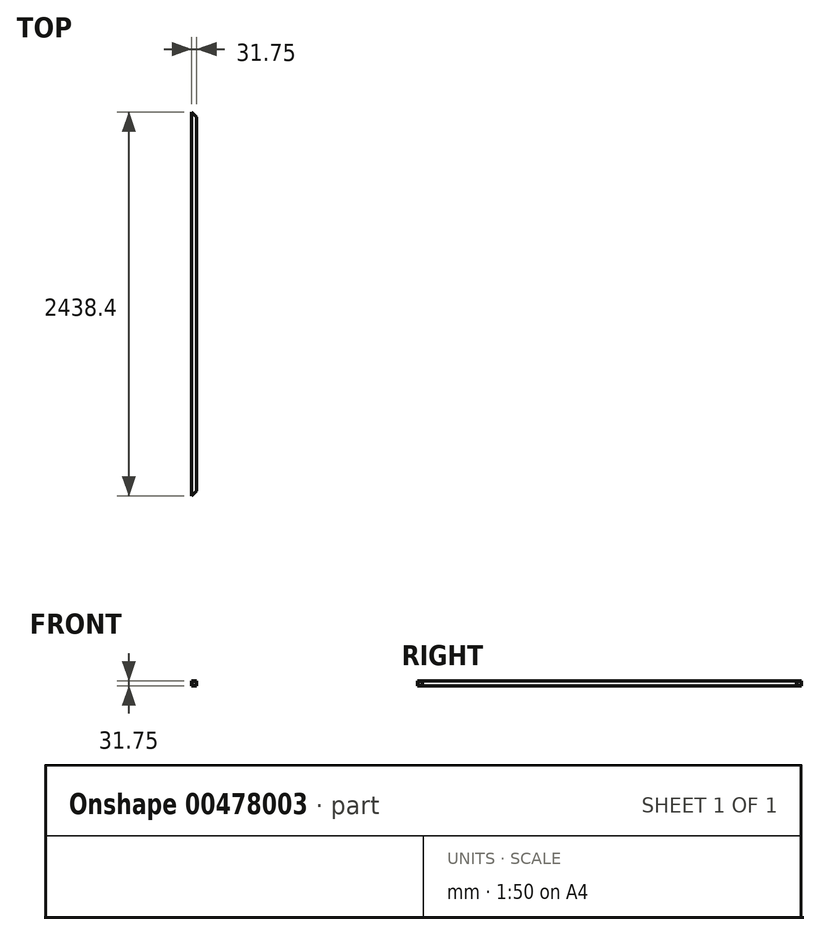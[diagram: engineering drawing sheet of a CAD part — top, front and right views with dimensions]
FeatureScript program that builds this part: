
annotation { "Feature Type Name" : "Feature", "Feature Type Description" : "" }
export const myFeature = defineFeature(function(context is Context, id is Id, definition is map)
    precondition{}
    {
        {
            var Q0;
            Q0=qCreatedBy(makeId("Front.planeOp"),FACE);
            var sketch = newSketch(context, id + "F0", { "sketchPlane" : qUnion([Q0])});
            skLineSegment(sketch, "E0.bottom", {"start": v(-64.17, 32) * mm, "end": v(-32.42, 32) * mm});
            skLineSegment(sketch, "E0.top", {"start": v(-64.17, 0.25) * mm, "end": v(-32.42, 0.25) * mm});
            skLineSegment(sketch, "E0.left", {"start": v(-64.17, 32) * mm, "end": v(-64.17, 0.25) * mm});
            skLineSegment(sketch, "E0.right", {"start": v(-32.42, 32) * mm, "end": v(-32.42, 0.25) * mm});
            skLineSegment(sketch, "E1.0", {"start": v(-34.53, 29.89) * mm, "end": v(-34.53, 2.35) * mm});
            skLineSegment(sketch, "E1.1", {"start": v(-62.06, 29.89) * mm, "end": v(-34.53, 29.89) * mm});
            skLineSegment(sketch, "E1.2", {"start": v(-62.06, 29.89) * mm, "end": v(-62.06, 2.35) * mm});
            skLineSegment(sketch, "E1.3", {"start": v(-62.06, 2.35) * mm, "end": v(-34.53, 2.35) * mm});
            skSolve(sketch);
        }
        {
            var Q0;
            Q0=qSketchRegion(id+"F0",true);
            extrude(context, id + "F1", {"entities" : qUnion([Q0]), "depth" : 2438.4 * mm});
        }
        {
            var Q0;
            Q0=makeQuery(id+"F1.opExtrude","SWEPT_FACE",FACE,{"disambiguationData":[OSD([sQuery(id+"F0.wireOp",EDGE,"E0.bottom")])]});
            var sketch = newSketch(context, id + "F2", { "sketchPlane" : qUnion([Q0])});
            skLineSegment(sketch, "E2", {"start": v(-64.17, 0) * mm, "end": v(-32.42, -31.75) * mm});
            skLineSegment(sketch, "E3.MirrorCS", {"start": v(-64.17, -2438.4) * mm, "end": v(-32.39, -2406.62) * mm});
            skSolve(sketch);
        }
        {
            var Q0;
            Q0=qSketchRegion(id+"F2",true);
            var Q1;
            {var subQ0=sQuery(id+"F2.wireOp",EDGE,"E2");Q1=makeQuery(id+"F2.imprint","IMPRINT",FACE,{"disambiguationData":[TD([[makeQuery(id+"F2.imprint","IMPRINT",EDGE,{"derivedFrom":subQ0}),1.0]])]});}
            var Q2;
            {var subQ0=sQuery(id+"F2.wireOp",EDGE,"E3.MirrorCS");Q2=makeQuery(id+"F2.imprint","IMPRINT",FACE,{"disambiguationData":[TD([[makeQuery(id+"F2.imprint","IMPRINT",EDGE,{"derivedFrom":subQ0}),-1.0]])]});}
            extrude(context, id + "F3", {"entities" : qUnion([Q0, Q1, Q2]), "operationType" : NewBodyOperationType.REMOVE, "oppositeDirection" : true, "depth" : 76.2 * mm});
        }
    });
